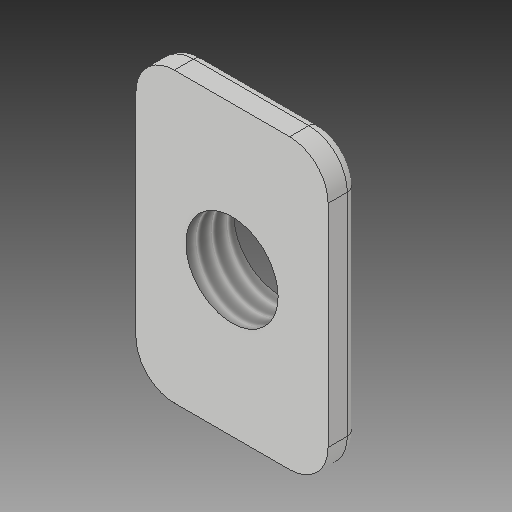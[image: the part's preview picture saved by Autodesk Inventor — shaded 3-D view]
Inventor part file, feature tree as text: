
AUTODESK INVENTOR PART (.ipt)
format: ipt  version: 2018 (Build 220112000, 112)  size: 160,256 bytes
history: native  units: mm
features: other x3, sketch x2
ambient origin geometry x8: Origin, YZ Plane, XZ Plane, XY Plane, X Axis, Y Axis, Z Axis, Center Point
bodies: Solid1 (feature_tree)
feature tree (5):
  other  "M5 Tee Nut-Generic.ipt"
  other  "Solid1::M5 Tee Nut-Generic.ipt"
  other  "TaggingFeature1"
  sketch  "Sketch1"  dims[d0=10.0mm]
  sketch  "Sketch2"
